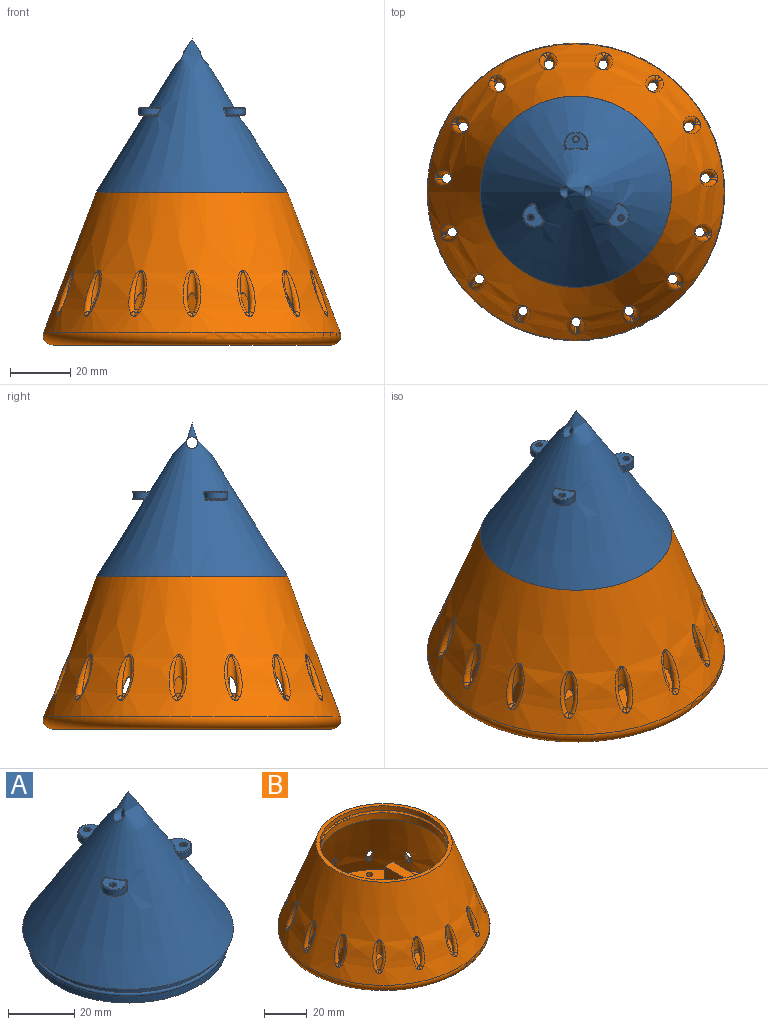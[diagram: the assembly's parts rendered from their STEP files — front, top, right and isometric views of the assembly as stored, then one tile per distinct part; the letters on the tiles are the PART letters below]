
ASSEMBLY  parts=2 mates=1
PART A: 54 faces, bbox 66x66x57.2 mm
  f0: cone r=0mm half-angle=32deg, axis (0,0,-1), area 5863.7mm2, adj f6,f8,f21,f23,f24,f25,f26,f28
  f1: cylinder r=29.84mm len=59.69mm, axis (0,0,1), area 476.3mm2, adj f3,f5
  f2: cylinder r=28.75mm len=57.51mm, axis (0,0,1), area 1147.3mm2, adj f3,f4
  f3: plane 59.69x59.69mm, normal (0,0,-1), area 200.7mm2, adj f1,f2
  f4: cone r=0mm half-angle=32deg, axis (0,0,-1), area 4877.5mm2, adj f2,f8
  f5: torus R=29.86mm, axis (0,0,-1), area 384.5mm2, adj f1,f7
  f6: plane 63.5x63.5mm, normal (0,0,-1), area 368.6mm2, adj f0,f7
  f7: cylinder r=29.84mm len=59.69mm, axis (0,0,1), area 476.3mm2, adj f5,f6
  f8: cylinder r=1.94mm len=10.63mm, axis (1,0,0), area 79.8mm2, adj f0,f4
  f9: cylinder r=3.81mm len=7.62mm, axis (0,0,-1), area 28.4mm2, adj f41,f44,f47,f50
  f10: plane 7.11x5.39mm, normal (0,0,1), area 26.9mm2, adj f44,f45,f53
  f11: plane 7.11x3.55mm, normal (0,0,-1), area 15.5mm2, adj f20,f46,f47
  f12: cylinder r=3.81mm len=7.6mm, axis (0,0,-1), area 28.4mm2, adj f22,f25,f26,f27
  f13: plane 7.11x6.67mm, normal (0,0,1), area 26.9mm2, adj f21,f22,f52
  f14: plane 6.63x5.33mm, normal (0,0,-1), area 15.5mm2, adj f19,f27,f30
  f15: cylinder r=3.81mm len=7.6mm, axis (0,0,-1), area 28.4mm2, adj f31,f34,f37,f40
  f16: plane 7.11x6.67mm, normal (0,0,1), area 26.9mm2, adj f36,f37,f51
  f17: plane 6.63x5.33mm, normal (0,0,-1), area 15.5mm2, adj f18,f34,f35
  f18: cylinder r=0.89mm len=2.29mm, axis (0,0,1), area 12.8mm2, adj f17,f51
  f19: cylinder r=0.89mm len=2.29mm, axis (0,0,1), area 12.8mm2, adj f14,f52
  f20: cylinder r=0.89mm len=2.29mm, axis (0,0,1), area 12.8mm2, adj f11,f53
  f21: torus R=14.43mm, axis (0,0,1), area 1.6mm2, adj f0,f13,f23,f24
  f22: torus R=3.56mm, axis (0,0,1), area 6.1mm2, adj f12,f13,f23,f24
  f23: bspline ~0.74x0.6mm, area 0.2mm2, adj f0,f21,f22,f25
  f24: bspline ~0.77x0.63mm, area 0.2mm2, adj f0,f21,f22,f26
  f25: bspline ~4.03x2.49mm, area 1mm2, adj f0,f12,f23,f28
  f26: bspline ~3.11x1.62mm, area 1mm2, adj f0,f12,f24,f29
  f27: torus R=3.56mm, axis (0,0,1), area 4.8mm2, adj f12,f14,f28,f29
  f28: bspline ~0.74x0.66mm, area 0.3mm2, adj f0,f25,f27,f30
  f29: bspline ~0.85x0.68mm, area 0.3mm2, adj f0,f26,f27,f30
  f30: torus R=16.33mm, axis (0,0,1), area 3.8mm2, adj f0,f14,f28,f29
  f31: bspline ~4.03x1.97mm, area 1mm2, adj f0,f15,f32,f33
  f32: bspline ~0.82x0.66mm, area 0.3mm2, adj f0,f31,f34,f35
  f33: bspline ~0.77x0.6mm, area 0.2mm2, adj f0,f31,f36,f37
  f34: torus R=3.56mm, axis (0,0,1), area 4.8mm2, adj f15,f17,f32,f38
  f35: torus R=16.33mm, axis (0,0,1), area 3.8mm2, adj f0,f17,f32,f38
  f36: torus R=14.43mm, axis (0,0,1), area 1.6mm2, adj f0,f16,f33,f39
  f37: torus R=3.56mm, axis (0,0,1), area 6.1mm2, adj f15,f16,f33,f39
  f38: bspline ~0.76x0.68mm, area 0.3mm2, adj f0,f34,f35,f40
  f39: bspline ~0.75x0.63mm, area 0.2mm2, adj f0,f36,f37,f40
  f40: bspline ~3.11x1.93mm, area 1mm2, adj f0,f15,f38,f39
  f41: bspline ~3.11x2.01mm, area 1mm2, adj f0,f9,f42,f43
  f42: bspline ~0.75x0.55mm, area 0.2mm2, adj f0,f41,f44,f45
  f43: bspline ~0.72x0.68mm, area 0.3mm2, adj f0,f41,f46,f47
  f44: torus R=3.56mm, axis (0,0,1), area 6.1mm2, adj f9,f10,f42,f48
  f45: torus R=14.43mm, axis (0,0,1), area 1.6mm2, adj f0,f10,f42,f48
  f46: torus R=16.33mm, axis (0,0,1), area 3.8mm2, adj f0,f11,f43,f49
  f47: torus R=3.56mm, axis (0,0,1), area 4.8mm2, adj f9,f11,f43,f49
  f48: bspline ~0.76x0.6mm, area 0.2mm2, adj f0,f44,f45,f50
  f49: bspline ~0.68x0.66mm, area 0.3mm2, adj f0,f46,f47,f50
  f50: bspline ~4.03x2.55mm, area 1mm2, adj f0,f9,f48,f49
  f51: torus R=1.14mm, axis (0,0,1), area 2.5mm2, adj f16,f18
  f52: torus R=1.14mm, axis (0,0,1), area 2.5mm2, adj f13,f19
  f53: torus R=1.14mm, axis (0,0,1), area 2.5mm2, adj f10,f20
PART B: 106 faces, bbox 106.9x106.9x51.2 mm
  f0: bspline ~7x3.4mm, area 3.9mm2, adj f1,f37,f45,f105
  f1: bspline ~7x3.06mm, area 3.9mm2, adj f0,f37,f45,f105
  f2: bspline ~7x3.07mm, area 3.9mm2, adj f3,f37,f46,f104
  f3: bspline ~7x3.17mm, area 3.9mm2, adj f2,f37,f46,f104
  f4: bspline ~7x2.99mm, area 3.9mm2, adj f5,f37,f47,f103
  f5: bspline ~7x3.43mm, area 3.9mm2, adj f4,f37,f47,f103
  f6: bspline ~7x3.4mm, area 3.9mm2, adj f7,f37,f48,f102
  f7: bspline ~7x3.25mm, area 3.9mm2, adj f6,f37,f48,f102
  f8: bspline ~7x3.33mm, area 3.9mm2, adj f9,f37,f49,f101
  f9: bspline ~7x3.09mm, area 3.9mm2, adj f8,f37,f49,f101
  f10: bspline ~7x3.09mm, area 3.9mm2, adj f11,f37,f50,f100
  f11: bspline ~7x3.26mm, area 3.9mm2, adj f10,f37,f50,f100
  f12: bspline ~2.54x1.92mm, area 3.9mm2, adj f13,f37,f51,f99
  f13: bspline ~7x3.43mm, area 3.9mm2, adj f12,f37,f51,f99
  f14: bspline ~7x3.43mm, area 3.9mm2, adj f15,f37,f52,f98
  f15: bspline ~7x3.14mm, area 3.9mm2, adj f14,f37,f52,f98
  f16: bspline ~7x3.26mm, area 3.9mm2, adj f17,f37,f53,f97
  f17: bspline ~7x3.09mm, area 3.9mm2, adj f16,f37,f53,f97
  f18: bspline ~7x3.09mm, area 3.9mm2, adj f19,f37,f54,f96
  f19: bspline ~7x3.33mm, area 3.9mm2, adj f18,f37,f54,f96
  f20: bspline ~7x3.25mm, area 3.9mm2, adj f21,f37,f55,f95
  f21: bspline ~7x3.39mm, area 3.9mm2, adj f20,f37,f55,f95
  f22: bspline ~7x3.43mm, area 3.9mm2, adj f23,f37,f56,f94
  f23: bspline ~7x2.99mm, area 3.9mm2, adj f22,f37,f56,f94
  f24: bspline ~7x3.17mm, area 3.9mm2, adj f25,f37,f57,f93
  f25: bspline ~7x3.07mm, area 3.9mm2, adj f24,f37,f57,f93
  f26: bspline ~2.51x1.91mm, area 3.9mm2, adj f27,f37,f58,f92
  f27: bspline ~7x3.41mm, area 3.8mm2, adj f26,f37,f58,f92
  f28: bspline ~7x3.33mm, area 3.9mm2, adj f29,f37,f59,f91
  f29: bspline ~7x3.34mm, area 3.9mm2, adj f28,f37,f59,f91
  f30: plane 6.43x3.4mm, normal (0,0,-1), area 6.9mm2, adj f44,f87,f89
  f31: cylinder r=25.4mm len=50.8mm, axis (0,0,-1), area 357.1mm2, adj f33,f75,f79
  f32: cylinder r=12.7mm len=25.4mm, axis (0,0,-1), area 50.7mm2, adj f44,f79
  f33: plane 94.27x94.27mm, normal (0,0,1), area 4154.9mm2, adj f31,f39,f60,f61,f62,f63,f64,f65
  f34: cylinder r=29.84mm len=59.69mm, axis (0,0,1), area 452.6mm2, adj f35,f38
  f35: plane 63.5x63.5mm, normal (0,0,1), area 368.6mm2, adj f34,f37
  f36: plane 92.44x92.44mm, normal (0,0,-1), area 4590.4mm2, adj f42,f44,f60,f61,f62,f63,f64,f65
  f37: cone r=31.75mm half-angle=20.6deg, axis (0,0,-1), area 11520mm2, adj f0,f1,f2,f3,f4,f5,f6,f7
  f38: torus R=29.82mm, axis (0,0,1), area 446.6mm2, adj f34,f41
  f39: cone r=29.37mm half-angle=20.6deg, axis (0,0,-1), area 10439.6mm2, adj f33,f40,f45,f46,f47,f48,f49,f50
  f40: plane 63.79x63.79mm, normal (0,0,-1), area 397.6mm2, adj f39,f41
  f41: cylinder r=29.84mm len=59.69mm, axis (0,0,1), area 690.7mm2, adj f38,f40
  f42: torus R=46.22mm, axis (0,0,1), area 1864.7mm2, adj f36,f37
  f43: plane 50.8x19.05mm, normal (0,0,1), area 571.9mm2, adj f75,f76,f77,f78,f85,f86
  f44: torus R=17.78mm, axis (0,0,1), area 729.3mm2, adj f30,f32,f36,f88,f90
  f45: cylinder r=1.59mm len=15.48mm, axis (0,0,-1), area 35.2mm2, adj f0,f1,f39,f105
  f46: cylinder r=1.59mm len=15.47mm, axis (0,0,-1), area 35.5mm2, adj f2,f3,f39,f104
  f47: cylinder r=1.59mm len=15.47mm, axis (0,0,-1), area 35.5mm2, adj f4,f5,f39,f103
  f48: cylinder r=1.59mm len=15.47mm, axis (0,0,-1), area 35.1mm2, adj f6,f7,f39,f102
  f49: cylinder r=1.59mm len=15.47mm, axis (0,0,-1), area 35.5mm2, adj f8,f9,f39,f101
  f50: cylinder r=1.59mm len=15.45mm, axis (0,0,-1), area 35.4mm2, adj f10,f11,f39,f100
  f51: cylinder r=1.59mm len=15.47mm, axis (0,0,-1), area 35.5mm2, adj f12,f13,f39,f99
  f52: cylinder r=1.59mm len=15.47mm, axis (0,0,-1), area 35.4mm2, adj f14,f15,f39,f98
  f53: cylinder r=1.59mm len=15.47mm, axis (0,0,-1), area 35.4mm2, adj f16,f17,f39,f97
  f54: cylinder r=1.59mm len=15.47mm, axis (0,0,-1), area 35.5mm2, adj f18,f19,f39,f96
  f55: cylinder r=1.59mm len=15.47mm, axis (0,0,-1), area 35.6mm2, adj f20,f21,f39,f95
  f56: cylinder r=1.59mm len=15.47mm, axis (0,0,-1), area 35.5mm2, adj f22,f23,f39,f94
  f57: cylinder r=1.59mm len=15.47mm, axis (0,0,-1), area 35.4mm2, adj f24,f25,f39,f93
  f58: cylinder r=1.59mm len=15.48mm, axis (0,0,-1), area 35.6mm2, adj f26,f27,f39,f92
  f59: cylinder r=1.59mm len=15.47mm, axis (0,0,-1), area 35.2mm2, adj f28,f29,f39,f91
  f60: cylinder r=1.59mm len=3.18mm, axis (0,0,-1), area 25.3mm2, adj f33,f36
  f61: cylinder r=1.59mm len=3.18mm, axis (0,0,-1), area 25.3mm2, adj f33,f36
  f62: cylinder r=1.59mm len=3.18mm, axis (0,0,-1), area 25.3mm2, adj f33,f36
  f63: cylinder r=1.59mm len=3.18mm, axis (0,0,-1), area 25.3mm2, adj f33,f36
  f64: cylinder r=1.59mm len=3.18mm, axis (0,0,-1), area 25.3mm2, adj f33,f36
  f65: cylinder r=1.59mm len=3.18mm, axis (0,0,-1), area 25.3mm2, adj f33,f36
  f66: cylinder r=1.59mm len=3.18mm, axis (0,0,-1), area 25.3mm2, adj f33,f36
  f67: cylinder r=1.59mm len=3.18mm, axis (0,0,-1), area 25.3mm2, adj f33,f36
  f68: cylinder r=1.59mm len=3.18mm, axis (0,0,-1), area 25.3mm2, adj f33,f36
  f69: cylinder r=1.59mm len=3.18mm, axis (0,0,-1), area 25.3mm2, adj f33,f36
  f70: cylinder r=1.59mm len=3.18mm, axis (0,0,-1), area 25.3mm2, adj f33,f36
  f71: cylinder r=1.59mm len=3.18mm, axis (0,0,-1), area 25.3mm2, adj f33,f36
  f72: cylinder r=1.59mm len=3.18mm, axis (0,0,-1), area 25.3mm2, adj f33,f36
  f73: cylinder r=1.59mm len=3.18mm, axis (0,0,-1), area 25.3mm2, adj f33,f36
  f74: cylinder r=1.59mm len=3.18mm, axis (0,0,-1), area 25.3mm2, adj f33,f36
  f75: plane 50.8x9.14mm, normal (1,0,0), area 335.5mm2, adj f31,f33,f43,f76,f78,f79
  f76: plane 19.05x9.14mm, normal (0,1,0), area 174.2mm2, adj f33,f43,f75,f77
  f77: plane 50.8x9.14mm, normal (-1,0,0), area 464.5mm2, adj f33,f43,f76,f78
  f78: plane 19.05x9.14mm, normal (0,-1,0), area 174.2mm2, adj f33,f43,f75,f77
  f79: plane 50.8x40.64mm, normal (0,0,1), area 1088.2mm2, adj f31,f32,f75,f81,f82,f83,f84
  f80: plane 25.4x5.64mm, normal (0,0,1), area 143.4mm2, adj f81,f82,f83,f84
  f81: plane 18.67x5.64mm, normal (0,-1,0), area 105.4mm2, adj f79,f80,f82,f84
  f82: plane 25.4x18.67mm, normal (1,0,0), area 474.2mm2, adj f79,f80,f81,f83
  f83: plane 18.67x5.64mm, normal (0,1,0), area 105.4mm2, adj f79,f80,f82,f84
  f84: plane 25.4x18.67mm, normal (-1,0,0), area 474.2mm2, adj f79,f80,f81,f83
  f85: cylinder r=7.94mm len=15.88mm, axis (0,0,1), area 335mm2, adj f43,f87,f88
  f86: cylinder r=7.94mm len=15.88mm, axis (0,0,1), area 335mm2, adj f43,f89,f90
  f87: torus R=13.02mm, axis (0,0,1), area 403.2mm2, adj f30,f36,f85,f88
  f88: bspline ~13x10.02mm, area 55.4mm2, adj f44,f85,f87
  f89: torus R=13.02mm, axis (0,0,1), area 403.2mm2, adj f30,f36,f86,f90
  f90: bspline ~12.98x10mm, area 55.4mm2, adj f44,f86,f89
  f91: bspline ~14.87x5.88mm, area 56.4mm2, adj f28,f29,f37,f59
  f92: bspline ~14.96x5.85mm, area 56.5mm2, adj f26,f27,f37,f58
  f93: bspline ~14.89x5.81mm, area 56.3mm2, adj f24,f25,f37,f57
  f94: bspline ~14.7x5.86mm, area 56.4mm2, adj f22,f23,f37,f56
  f95: bspline ~14.69x5.88mm, area 56.4mm2, adj f20,f21,f37,f55
  f96: bspline ~14.75x5.84mm, area 56.4mm2, adj f18,f19,f37,f54
  f97: bspline ~14.79x5.82mm, area 56.4mm2, adj f16,f17,f37,f53
  f98: bspline ~14.72x5.87mm, area 56.4mm2, adj f14,f15,f37,f52
  f99: bspline ~14.78x5.87mm, area 56.4mm2, adj f12,f13,f37,f51
  f100: bspline ~14.91x5.82mm, area 56.4mm2, adj f10,f11,f37,f50
  f101: bspline ~14.78x5.84mm, area 56.4mm2, adj f8,f9,f37,f49
  f102: bspline ~14.99x5.88mm, area 56.5mm2, adj f6,f7,f37,f48
  f103: bspline ~14.66x5.86mm, area 56.4mm2, adj f4,f5,f37,f47
  f104: bspline ~14.75x5.81mm, area 56.4mm2, adj f2,f3,f37,f46
  f105: bspline ~14.82x5.85mm, area 56.4mm2, adj f0,f1,f37,f45
PLACE A t=(-30.76,-7.44,4.02)mm
PLACE B t=(-30.76,-7.44,-46.78)mm
MATE fastened A.f0 <-> B.f31  axis (0,0,-1) through (-30.76,-7.44,4.02)mm
